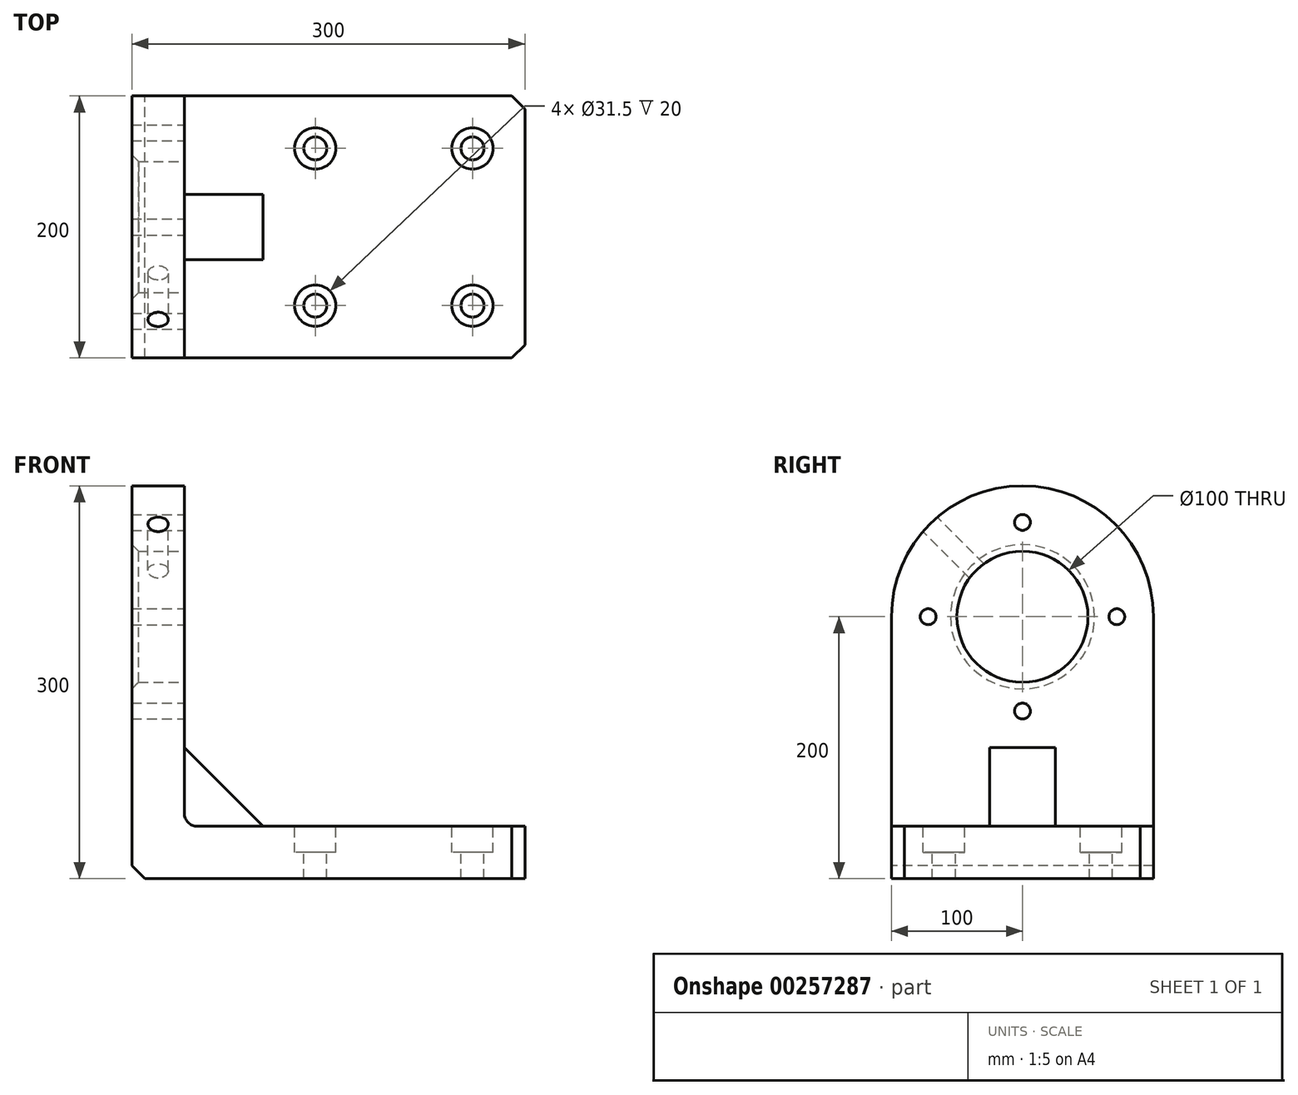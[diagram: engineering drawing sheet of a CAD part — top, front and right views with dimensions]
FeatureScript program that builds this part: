
annotation { "Feature Type Name" : "Feature", "Feature Type Description" : "" }
export const myFeature = defineFeature(function(context is Context, id is Id, definition is map)
    precondition{}
    {
        {
            var Q0;
            Q0=qCreatedBy(makeId("Front.planeOp"),FACE);
            var sketch = newSketch(context, id + "F0", { "sketchPlane" : qUnion([Q0])});
            skLineSegment(sketch, "E0", {"start": v(0, 300) * mm, "end": v(0, 0) * mm});
            skLineSegment(sketch, "E1", {"start": v(0, 0) * mm, "end": v(300, 0) * mm});
            skLineSegment(sketch, "E2", {"start": v(300, 0) * mm, "end": v(300, 40) * mm});
            skLineSegment(sketch, "E3", {"start": v(300, 40) * mm, "end": v(40, 40) * mm});
            skLineSegment(sketch, "E4", {"start": v(40, 40) * mm, "end": v(40, 300) * mm});
            skLineSegment(sketch, "E5", {"start": v(40, 300) * mm, "end": v(0, 300) * mm});
            skSolve(sketch);
        }
        {
            var Q0;
            Q0=makeQuery(id+"F0.imprint","IMPRINT",FACE,{"disambiguationData":[TD([[makeQuery(id+"F0.imprint","IMPRINT",EDGE,{"derivedFrom":sQuery(id+"F0.wireOp",EDGE,"E0")}),1.0]])]});
            extrude(context, id + "F1", {"entities" : qUnion([Q0]), "depth" : 200 * mm, "symmetric" : true});
        }
        {
            var Q0;
            Q0=makeQuery(id+"F1.opExtrude","CAP_EDGE",EDGE,{"disambiguationData":[OSD([sQuery(id+"F0.wireOp",EDGE,"E5")])],"isStart":false});
            var Q1;
            Q1=makeQuery(id+"F1.opExtrude","CAP_EDGE",EDGE,{"disambiguationData":[OSD([sQuery(id+"F0.wireOp",EDGE,"E5")])],"isStart":true});
            fillet(context, id + "F2", {"entities" : qUnion([Q0, Q1]), "radius" : 100 * mm, "tangentPropagation" : true, "allowEdgeOverflow" : false});
        }
        {
            var Q0;
            Q0=makeQuery(id+"F1.opExtrude","CAP_EDGE",EDGE,{"disambiguationData":[OSD([sQuery(id+"F0.wireOp",EDGE,"E2")])],"isStart":false});
            var Q1;
            Q1=makeQuery(id+"F1.opExtrude","CAP_EDGE",EDGE,{"disambiguationData":[OSD([sQuery(id+"F0.wireOp",EDGE,"E2")])],"isStart":true});
            var Q2;
            Q2=makeQuery(id+"F1.opExtrude","SWEPT_EDGE",EDGE,{"disambiguationData":[OSD([sQuery(id+"F0.wireOp",EDGE,"E0"),sQuery(id+"F0.wireOp",EDGE,"E1")])]});
            chamfer(context, id + "F3", {"entities" : qUnion([Q0, Q1, Q2]), "width" : 10 * mm, "tangentPropagation" : true});
        }
        {
            var Q0;
            Q0=qCreatedBy(makeId("Front.planeOp"),FACE);
            var sketch = newSketch(context, id + "F4", { "sketchPlane" : qUnion([Q0])});
            skLineSegment(sketch, "E6.0", {"start": v(40, 40) * mm, "end": v(40, 200) * mm});
            skLineSegment(sketch, "E7.0.0", {"start": v(0, 200) * mm, "end": v(0, 10) * mm});
            skLineSegment(sketch, "E7.0.1", {"start": v(0, 10) * mm, "end": v(10, 0) * mm});
            skLineSegment(sketch, "E7.0.2", {"start": v(10, 0) * mm, "end": v(290, 0) * mm});
            skLineSegment(sketch, "E7.0.3", {"start": v(290, 0) * mm, "end": v(290, 40) * mm});
            skLineSegment(sketch, "E7.0.4", {"start": v(290, 40) * mm, "end": v(40, 40) * mm});
            skLineSegment(sketch, "E7.0.6", {"start": v(40, 200) * mm, "end": v(0, 200) * mm});
            skLineSegment(sketch, "E8", {"start": v(40, 100) * mm, "end": v(100, 40) * mm});
            skSolve(sketch);
        }
        {
            var Q0;
            {var subQ3=sQuery(id+"F4.wireOp",EDGE,"E8");Q0=makeQuery(id+"F4.imprint","IMPRINT",FACE,{"disambiguationData":[TD([[makeQuery(id+"F4.imprint","IMPRINT",EDGE,{"derivedFrom":subQ3}),-1.0]])]});}
            extrude(context, id + "F5", {"entities" : qUnion([Q0]), "operationType" : NewBodyOperationType.ADD, "depth" : 50 * mm, "symmetric" : true});
        }
        {
            var Q0;
            Q0=makeQuery(id+"F1.opExtrude","SWEPT_FACE",FACE,{"disambiguationData":[OSD([sQuery(id+"F0.wireOp",EDGE,"E4")])]});
            var sketch = newSketch(context, id + "F6", { "sketchPlane" : qUnion([Q0])});
            skArc(sketch, "E9.0", {"start": v(100, 200) * mm, "mid": v(0, 300) * mm, "end": v(-100, 200) * mm, "construction": true});
            skCircle(sketch, "E10", {"center": v(0, 200) * mm, "radius": 50 * mm});
            skCircle(sketch, "E11", {"center": v(0, 200) * mm, "radius": 72 * mm, "construction": true});
            skPoint(sketch, "E12", {"position": v(0, 272) * mm});
            skPoint(sketch, "E13", {"position": v(0, 128) * mm});
            skPoint(sketch, "E14", {"position": v(72, 200) * mm});
            skPoint(sketch, "E15", {"position": v(-72, 200) * mm});
            skLineSegment(sketch, "E16", {"start": v(0, 200) * mm, "end": v(-70.71, 270.71) * mm, "construction": true});
            skSolve(sketch);
        }
        {
            var Q0;
            Q0=makeQuery(id+"F6.imprint","IMPRINT",FACE,{"disambiguationData":[TD([[makeQuery(id+"F6.imprint","IMPRINT",EDGE,{"derivedFrom":sQuery(id+"F6.wireOp",EDGE,"E10")}),1.0]])]});
            extrude(context, id + "F7", {"entities" : qUnion([Q0]), "operationType" : NewBodyOperationType.REMOVE, "endBound" : BoundingType.THROUGH_ALL, "oppositeDirection" : true, "depth" : 25 * mm});
        }
        {
            var Q0;
            Q0=sQuery(id+"F6.wireOp",VERTEX,"E16.end");
            var Q1;
            Q1=sQuery(id+"F6.wireOp",EDGE,"E16");
            cPlane(context, id + "F8", {"entities" : qUnion([Q0, Q1]), "cplaneType" : CPlaneType.LINE_POINT, "offset" : 25 * mm, "width" : 150 * mm, "height" : 150 * mm});
        }
        {
            var Q0;
            Q0=qCreatedBy(id+"F8.planeOp",FACE);
            var sketch = newSketch(context, id + "F9", { "sketchPlane" : qUnion([Q0])});
            skPoint(sketch, "E17.0", {"position": v(40, 141.42) * mm});
            skLineSegment(sketch, "E18.0", {"start": v(0, 70.71) * mm, "end": v(0, 241.42) * mm, "construction": true});
            skLineSegment(sketch, "E19", {"start": v(40, 141.42) * mm, "end": v(0, 141.42) * mm, "construction": true});
            skPoint(sketch, "E20", {"position": v(20, 141.42) * mm});
            skSolve(sketch);
        }
        {
            var Q0;
            Q0=sQuery(id+"F6.wireOp",VERTEX,"E12");
            var Q1;
            Q1=sQuery(id+"F6.wireOp",VERTEX,"E14");
            var Q2;
            Q2=sQuery(id+"F6.wireOp",VERTEX,"E13");
            var Q3;
            Q3=sQuery(id+"F6.wireOp",VERTEX,"E15");
            var Q4;
            Q4=makeQuery(id+"F1.opExtrude","SWEPT_BODY",BODY,{"disambiguationData":[OSD([sQuery(id+"F0.wireOp",EDGE,"E0"),sQuery(id+"F0.wireOp",EDGE,"E1"),sQuery(id+"F0.wireOp",EDGE,"E2"),sQuery(id+"F0.wireOp",EDGE,"E3"),sQuery(id+"F0.wireOp",EDGE,"E4"),sQuery(id+"F0.wireOp",EDGE,"E5")])]});
            hole(context, id + "F10", {"style" : HoleStyle.SIMPLE, "endStyle" : HoleEndStyle.THROUGH, "standardTappedOrClearance" : lookupTablePath({ "standard" : "ISO", "engagement" : "75%", "pitch" : "2 mm", "size" : "M14", "type" : "Tapped" }), "standardBlindInLast" : lookupTablePath({ "standard" : "ISO", "engagement" : "75%", "pitch" : "2 mm", "size" : "M14", "type" : "Tapped" }), "holeDiameter" : 12.1 * mm, "showTappedDepth" : true, "tappedDepth" : 12 * mm, "tapClearance" : 3, "locations" : qUnion([Q0, Q1, Q2, Q3]), "scope" : qUnion([Q4]), "majorDiameter" : 14 * mm});
        }
        {
            var Q0;
            Q0=sQuery(id+"F9.wireOp",VERTEX,"E20");
            var Q1;
            Q1=makeQuery(id+"F1.opExtrude","SWEPT_BODY",BODY,{"disambiguationData":[OSD([sQuery(id+"F0.wireOp",EDGE,"E0"),sQuery(id+"F0.wireOp",EDGE,"E1"),sQuery(id+"F0.wireOp",EDGE,"E2"),sQuery(id+"F0.wireOp",EDGE,"E3"),sQuery(id+"F0.wireOp",EDGE,"E4"),sQuery(id+"F0.wireOp",EDGE,"E5")])]});
            hole(context, id + "F11", {"style" : HoleStyle.SIMPLE, "endStyle" : HoleEndStyle.BLIND, "standardTappedOrClearance" : lookupTablePath({ "standard" : "ISO", "fit" : "Normal", "size" : "M14", "type" : "Clearance" }), "standardBlindInLast" : lookupTablePath({ "fit" : "Standard", "standard" : "ISO", "size" : "M14", "type" : "Clearance" }), "holeDiameter" : 15.5 * mm, "holeDepth" : 70 * mm, "tappedDepth" : 12 * mm, "tapClearance" : 3, "locations" : qUnion([Q0]), "scope" : qUnion([Q1])});
        }
        {
            var Q0;
            Q0=makeQuery(id+"F1.opExtrude","SWEPT_FACE",FACE,{"disambiguationData":[OSD([sQuery(id+"F0.wireOp",EDGE,"E3")])]});
            var sketch = newSketch(context, id + "F12", { "sketchPlane" : qUnion([Q0])});
            skLineSegment(sketch, "E21.bottom", {"start": v(260, 60) * mm, "end": v(140, 60) * mm, "construction": true});
            skLineSegment(sketch, "E21.top", {"start": v(260, -60) * mm, "end": v(140, -60) * mm, "construction": true});
            skLineSegment(sketch, "E21.left", {"start": v(260, 60) * mm, "end": v(260, -60) * mm, "construction": true});
            skLineSegment(sketch, "E21.right", {"start": v(140, 60) * mm, "end": v(140, -60) * mm, "construction": true});
            skLineSegment(sketch, "E22", {"start": v(260, 0) * mm, "end": v(300, 0) * mm, "construction": true});
            skPoint(sketch, "E23", {"position": v(140, 60) * mm});
            skPoint(sketch, "E24", {"position": v(260, 60) * mm});
            skPoint(sketch, "E25", {"position": v(260, -60) * mm});
            skPoint(sketch, "E26", {"position": v(140, -60) * mm});
            skSolve(sketch);
        }
        {
            var Q0;
            Q0=sQuery(id+"F12.wireOp",VERTEX,"E26");
            var Q1;
            Q1=sQuery(id+"F12.wireOp",VERTEX,"E23");
            var Q2;
            Q2=sQuery(id+"F12.wireOp",VERTEX,"E24");
            var Q3;
            Q3=sQuery(id+"F12.wireOp",VERTEX,"E25");
            var Q4;
            Q4=makeQuery(id+"F1.opExtrude","SWEPT_BODY",BODY,{"disambiguationData":[OSD([sQuery(id+"F0.wireOp",EDGE,"E0"),sQuery(id+"F0.wireOp",EDGE,"E1"),sQuery(id+"F0.wireOp",EDGE,"E2"),sQuery(id+"F0.wireOp",EDGE,"E3"),sQuery(id+"F0.wireOp",EDGE,"E4"),sQuery(id+"F0.wireOp",EDGE,"E5")])]});
            hole(context, id + "F13", {"style" : HoleStyle.C_BORE, "endStyle" : HoleEndStyle.THROUGH, "holeDiameter" : 17.5 * mm, "cBoreDiameter" : 31.5 * mm, "cBoreDepth" : 20 * mm, "tappedDepth" : 12 * mm, "tapClearance" : 3, "locations" : qUnion([Q0, Q1, Q2, Q3]), "scope" : qUnion([Q4])});
        }
        {
            var Q0;
            Q0=makeQuery(id+"F7.boolean.opBoolean","COPY",EDGE,{"derivedFrom":makeQuery(id+"F7.opExtrude","CAP_EDGE",EDGE,{"disambiguationData":[OSD([sQuery(id+"F6.wireOp",EDGE,"E10")])],"isStart":true})});
            var Q1;
            Q1=makeQuery(id+"F7.boolean.opBoolean","INTERSECT",EDGE,{"derivedFrom":[makeQuery(id+"F1.opExtrude","SWEPT_FACE",FACE,{"disambiguationData":[OSD([sQuery(id+"F0.wireOp",EDGE,"E0")])]}),makeQuery(id+"F7.opExtrude","SWEPT_FACE",FACE,{"disambiguationData":[OSD([sQuery(id+"F6.wireOp",EDGE,"E10")])]})]});
            chamfer(context, id + "F14", {"entities" : qUnion([Q0, Q1]), "width" : 5 * mm, "tangentPropagation" : true});
        }
        {
            var Q0;
            {var subQ0=sQuery(id+"F0.wireOp",EDGE,"E4");var subQ1=sQuery(id+"F0.wireOp",EDGE,"E3");Q0=makeQuery(id+"F5.boolean.opBoolean","SPLIT",EDGE,{"disambiguationData":[TD([makeQuery(id+"F5.opExtrude","CAP_FACE",FACE,{"disambiguationData":[OSD([sQuery(id+"F4.wireOp",EDGE,"E7.0.4"),sQuery(id+"F4.wireOp",EDGE,"E6.0"),sQuery(id+"F4.wireOp",EDGE,"E8")])],"isStart":false})])],"derivedFrom":makeQuery(id+"F1.opExtrude","SWEPT_EDGE",EDGE,{"disambiguationData":[OSD([subQ1,subQ0])]})});}
            var Q1;
            {var subQ0=sQuery(id+"F0.wireOp",EDGE,"E4");var subQ1=sQuery(id+"F0.wireOp",EDGE,"E3");Q1=makeQuery(id+"F5.boolean.opBoolean","SPLIT",EDGE,{"disambiguationData":[TD([makeQuery(id+"F5.opExtrude","CAP_FACE",FACE,{"disambiguationData":[OSD([sQuery(id+"F4.wireOp",EDGE,"E7.0.4"),sQuery(id+"F4.wireOp",EDGE,"E6.0"),sQuery(id+"F4.wireOp",EDGE,"E8")])],"isStart":true})])],"derivedFrom":makeQuery(id+"F1.opExtrude","SWEPT_EDGE",EDGE,{"disambiguationData":[OSD([subQ1,subQ0])]})});}
            fillet(context, id + "F15", {"entities" : qUnion([Q0, Q1]), "radius" : 10 * mm, "tangentPropagation" : true, "allowEdgeOverflow" : false});
        }
    });
